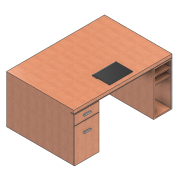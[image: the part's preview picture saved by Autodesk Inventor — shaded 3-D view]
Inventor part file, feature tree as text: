
AUTODESK INVENTOR PART (.ipt)
format: ipt  version: 2020.2 (Build 242310000, 310)  size: 302,080 bytes
history: native  units: mm
features: plane x13, sketch x12, extrude x10, shell x1, loft x1
ambient origin geometry x8: Origin, YZ Plane, XZ Plane, XY Plane, X Axis, Y Axis, Z Axis, Center Point
bodies: Solid1 (feature_tree), Solid2 (feature_tree), Solid3 (feature_tree), Solid6 (feature_tree)
feature tree (37):
  extrude  "Extrusion1"  Depth=1600.0mm
  plane  "Work Plane1"
  extrude  "Extrusion2"  Depth=400.0mm
  plane  "Work Plane2"
  extrude  "Extrusion3"  Depth=720.0mm TaperAngle=0.0deg
  plane  "Work Plane3"
  extrude  "Extrusion4"  Depth=1050.0mm
  plane  "Work Plane4"
  plane  "Work Plane5"
  sketch  "Sketch6"  dims[d9=60.0mm d10=0.0mm d11=10.0mm]
  extrude  "Extrusion5"  Depth=10.0mm
  extrude  "Extrusion6"  TaperAngle=0.0deg  [1 undecoded]
  plane  "Work Plane6"
  sketch  "Sketch9"  dims[d16=5.0mm d17=10.0mm d18=0.0mm]
  shell  "Shell1"  Thickness=155.0mm
  extrude  "Extrusion7"  Depth=10.0mm TaperAngle=0.0deg
  plane  "Work Plane7"
  extrude  "Extrusion8"  TaperAngle=0.0deg  [1 undecoded]
  plane  "Work Plane13"
  sketch  "Sketch16"  dims[d30=20.0mm d33=20.0mm]
  plane  "Work Plane14"
  loft  "Loft2"
  plane  "Work Plane15"
  plane  "Work Plane16"
  extrude  "Extrusion11"  Depth=15.0mm TaperAngle=0.0deg
  plane  "Work Plane17"
  plane  "Work Plane18"
  extrude  "Extrusion12"  Depth=20.0mm
  sketch  "Sketch1"  dims[d0=1100.0mm d1=1600.0mm]
  sketch  "Sketch2"  dims[d2=85.0mm d3=400.0mm]
  sketch  "Sketch3"  dims[d4=300.0mm d5=720.0mm d6=0.0mm]
  sketch  "Sketch4"  dims[d7=0.0mm d8=1050.0mm]
  sketch  "Sketch7"  dims[d12=50.0mm d13=0.0mm d14=0.0mm d15=155.0mm]
  sketch  "Sketch10"  dims[d19=0.0mm d20=0.0mm]
  sketch  "Sketch17"  dims[d34=15.0mm d35=0.0mm d36=15.0mm d37=0.0mm]
  sketch  "Sketch19"  dims[d38=0.0mm d40=20.0mm]
  sketch  "Sketch20"  dims[d42=15.0mm d44=15.0mm d45=1100.0mm d46=0.0mm d47=0.0mm d48=9.0mm d49=0.0mm d75=0.0mm d77=360.0mm d78=10.0mm d83=10.0mm d84=0.0mm d85=90.0deg d86=0.0mm d87=90.0deg d88=0.0mm d89=0.0mm d91=380.0mm d92=0.0mm d93=0.0mm d94=7.0mm d95=0.0mm d50=0.872665mm]
note: 2 required parameter values undecoded (feature->parameter linkage not recoverable at this tier; creation-order binding heuristic only, values carry confidence <= 0.55)
